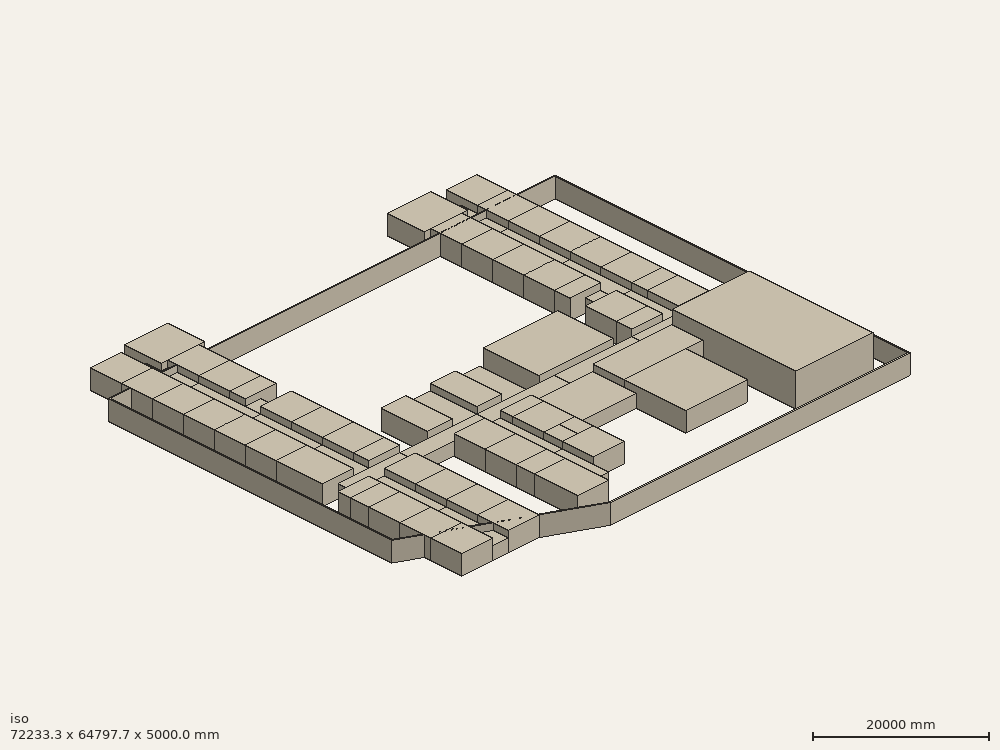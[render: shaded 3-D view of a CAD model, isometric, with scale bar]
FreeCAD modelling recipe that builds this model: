
FCSTD DOCUMENT  (FreeCAD 0.21R33771 (Git))
Label: WFCMaintest
License: All rights reserved
LicenseURL: http://en.wikipedia.org/wiki/All_rights_reserved
objects: Part::Box×79, Part::Compound×20, Sketcher::SketchObject×1, Part::FeaturePython×1
note: 101 computed .brp shape members not serialized (recipe doc carries the construction recipe); baked Part::Feature solids carry a one-line shape summary decoded from their .brp

FEATURE [Part::Box] Box  label="Cube"
  AttacherType = Attacher::AttachEngine3D
  Height = 3000
  Length = 5000
  Width = 5000
FEATURE [Part::Box] Box001  label="Cube001"
  AttacherType = Attacher::AttachEngine3D
  Height = 2000
  Length = 2500
  Placement = pos=(5000,0,0) rot=(0,0,1;0rad)
  Width = 10000
FEATURE [Part::Box] Box002  label="Cube002"
  AttacherType = Attacher::AttachEngine3D
  Height = 3000
  Length = 5000
  Placement = pos=(7500,0,0) rot=(0,0,1;0rad)
  Width = 5000
FEATURE [Part::Box] Box003  label="Cube003"
  AttacherType = Attacher::AttachEngine3D
  Height = 3000
  Length = 5000
  Placement = pos=(0,5000,0) rot=(0,0,1;0rad)
  Width = 5000
FEATURE [Part::Box] Box004  label="Cube004"
  AttacherType = Attacher::AttachEngine3D
  Height = 3000
  Length = 5000
  Placement = pos=(7500,5000,0) rot=(0,0,1;0rad)
  Width = 5000
FEATURE [Part::Compound] Compound  label="4C1"
  Links = -> [Box004,Box,Box001,Box002,Box003]
  Placement = pos=(0,30000,0) rot=(0,0,1;0rad)
FEATURE [Part::Box] Box005  label="Cube005"
  AttacherType = Attacher::AttachEngine3D
  Height = 3000
  Length = 5000
  Width = 5000
FEATURE [Part::Box] Box006  label="Cube006"
  AttacherType = Attacher::AttachEngine3D
  Height = 2000
  Length = 2500
  Placement = pos=(5000,0,0) rot=(0,0,1;0rad)
  Width = 10000
FEATURE [Part::Box] Box007  label="Cube007"
  AttacherType = Attacher::AttachEngine3D
  Height = 3000
  Length = 5000
  Placement = pos=(7500,0,0) rot=(0,0,1;0rad)
  Width = 5000
FEATURE [Part::Box] Box008  label="Cube008"
  AttacherType = Attacher::AttachEngine3D
  Height = 3000
  Length = 5000
  Placement = pos=(7500,5000,0) rot=(0,0,1;0rad)
  Width = 5000
FEATURE [Part::Box] Box009  label="Cube009"
  AttacherType = Attacher::AttachEngine3D
  Height = 3000
  Length = 5000
  Placement = pos=(0,5000,0) rot=(0,0,1;0rad)
  Width = 3000
FEATURE [Part::Box] Box010  label="Cube010"
  AttacherType = Attacher::AttachEngine3D
  Height = 3000
  Length = 5000
  Placement = pos=(0,8000,0) rot=(0,0,1;0rad)
  Width = 2000
FEATURE [Part::Compound] Compound001  label="3C1T1S"
  Links = -> [Box005,Box006,Box007,Box008,Box009,Box010]
  Placement = pos=(0,10000,0) rot=(0,0,1;0rad)
FEATURE [Part::Box] Box011  label="Cube011"
  AttacherType = Attacher::AttachEngine3D
  Height = 2000
  Length = 10000
  Placement = pos=(2500,0,0) rot=(0,0,1;0rad)
  Width = 2500
FEATURE [Part::Box] Box012  label="Cube012"
  AttacherType = Attacher::AttachEngine3D
  Height = 2000
  Length = 2500
  Placement = pos=(5000,2500,0) rot=(0,0,1;0rad)
  Width = 7500
FEATURE [Part::Box] Box013  label="Cube013"
  AttacherType = Attacher::AttachEngine3D
  Height = 3000
  Length = 5000
  Placement = pos=(0,2500,0) rot=(0,0,1;0rad)
  Width = 7500
FEATURE [Part::Box] Box014  label="Cube014"
  AttacherType = Attacher::AttachEngine3D
  Height = 3000
  Length = 5000
  Placement = pos=(7500,5000,0) rot=(0,0,1;0rad)
  Width = 5000
FEATURE [Part::Box] Box015  label="Cube015"
  AttacherType = Attacher::AttachEngine3D
  Height = 3000
  Length = 5000
  Placement = pos=(7500,2500,0) rot=(0,0,1;0rad)
  Width = 2500
FEATURE [Part::Compound] Compound002  label="T"
  Links = -> [Box011,Box012,Box013,Box014,Box015]
  Placement = pos=(0,20000,0) rot=(0,0,1;0rad)
FEATURE [Part::Box] Box016  label="Cube016"
  AttacherType = Attacher::AttachEngine3D
  Height = 2000
  Length = 10000
  Width = 2500
FEATURE [Part::Box] Box017  label="Cube017"
  AttacherType = Attacher::AttachEngine3D
  Height = 2000
  Length = 2500
  Placement = pos=(5000,2500,0) rot=(0,0,1;0rad)
  Width = 7500
FEATURE [Part::Box] Box018  label="Cube018"
  AttacherType = Attacher::AttachEngine3D
  Height = 3000
  Length = 5000
  Placement = pos=(0,5000,0) rot=(0,0,1;0rad)
  Width = 5000
FEATURE [Part::Box] Box019  label="Cube019"
  AttacherType = Attacher::AttachEngine3D
  Height = 3000
  Length = 5000
  Placement = pos=(7500,2500,0) rot=(0,0,1;0rad)
  Width = 5000
FEATURE [Part::Box] Box020  label="Cube020"
  AttacherType = Attacher::AttachEngine3D
  Height = 3000
  Length = 5000
  Placement = pos=(7500,7500,0) rot=(0,0,1;0rad)
  Width = 2500
FEATURE [Part::Box] Box021  label="Cube021"
  AttacherType = Attacher::AttachEngine3D
  Height = 3000
  Length = 5000
  Placement = pos=(0,2500,0) rot=(0,0,1;0rad)
  Width = 2500
FEATURE [Part::Compound] Compound003  label="TF"
  Links = -> [Box016,Box017,Box018,Box019,Box020,Box021]
  Placement = pos=(50000,20000,0) rot=(0,0,1;0rad)
FEATURE [Part::Box] Box022  label="Cube022"
  AttacherType = Attacher::AttachEngine3D
  Height = 3000
  Length = 5000
  Width = 5000
FEATURE [Part::Box] Box023  label="Cube023"
  AttacherType = Attacher::AttachEngine3D
  Height = 2000
  Length = 2500
  Placement = pos=(5000,0,0) rot=(0,0,1;0rad)
  Width = 10000
FEATURE [Part::Box] Box024  label="Cube024"
  AttacherType = Attacher::AttachEngine3D
  Height = 3000
  Length = 5000
  Placement = pos=(7500,2500,0) rot=(0,0,1;0rad)
  Width = 2500
FEATURE [Part::Box] Box025  label="Cube025"
  AttacherType = Attacher::AttachEngine3D
  Height = 3000
  Length = 5000
  Placement = pos=(0,5000,0) rot=(0,0,1;0rad)
  Width = 5000
FEATURE [Part::Box] Box026  label="Cube026"
  AttacherType = Attacher::AttachEngine3D
  Height = 3000
  Length = 5000
  Placement = pos=(7500,5000,0) rot=(0,0,1;0rad)
  Width = 5000
FEATURE [Part::Box] Box027  label="Cube027"
  AttacherType = Attacher::AttachEngine3D
  Height = 2000
  Length = 2500
  Placement = pos=(7500,0,0) rot=(0,0,1;0rad)
  Width = 2500
FEATURE [Part::Compound] Compound004  label="3C1S"
  Links = -> [Box026,Box022,Box023,Box024,Box025,Box027]
  Placement = pos=(0,40000,0) rot=(0,0,1;0rad)
FEATURE [Part::Box] Box028  label="Cube028"
  AttacherType = Attacher::AttachEngine3D
  Height = 3000
  Length = 5000
  Placement = pos=(7500,0,0) rot=(0,0,1;0rad)
  Width = 5000
FEATURE [Part::Box] Box029  label="Cube029"
  AttacherType = Attacher::AttachEngine3D
  Height = 2000
  Length = 2500
  Placement = pos=(5000,0,0) rot=(0,0,1;0rad)
  Width = 10000
FEATURE [Part::Box] Box030  label="Cube030"
  AttacherType = Attacher::AttachEngine3D
  Height = 3000
  Length = 5000
  Placement = pos=(0,2500,0) rot=(0,0,1;0rad)
  Width = 2500
FEATURE [Part::Box] Box031  label="Cube031"
  AttacherType = Attacher::AttachEngine3D
  Height = 3000
  Length = 5000
  Placement = pos=(0,5000,0) rot=(0,0,1;0rad)
  Width = 5000
FEATURE [Part::Box] Box032  label="Cube032"
  AttacherType = Attacher::AttachEngine3D
  Height = 3000
  Length = 5000
  Placement = pos=(7500,5000,0) rot=(0,0,1;0rad)
  Width = 5000
FEATURE [Part::Box] Box033  label="Cube033"
  AttacherType = Attacher::AttachEngine3D
  Height = 2000
  Length = 2500
  Placement = pos=(2500,0,0) rot=(0,0,1;0rad)
  Width = 2500
FEATURE [Part::Compound] Compound005  label="3C1SF"
  Links = -> [Box032,Box028,Box029,Box030,Box031,Box033]
  Placement = pos=(50000,30000,0) rot=(0,0,1;0rad)
FEATURE [Part::Box] Box034  label="Cube034"
  AttacherType = Attacher::AttachEngine3D
  Height = 3000
  Length = 5000
  Width = 5000
FEATURE [Part::Box] Box035  label="Cube035"
  AttacherType = Attacher::AttachEngine3D
  Height = 2000
  Length = 2500
  Placement = pos=(5000,0,0) rot=(0,0,1;0rad)
  Width = 7500
FEATURE [Part::Box] Box036  label="Cube036"
  AttacherType = Attacher::AttachEngine3D
  Height = 3000
  Length = 5000
  Placement = pos=(7500,0,0) rot=(0,0,1;0rad)
  Width = 5000
FEATURE [Part::Box] Box037  label="Cube037"
  AttacherType = Attacher::AttachEngine3D
  Height = 3000
  Length = 5000
  Placement = pos=(0,5000,0) rot=(0,0,1;0rad)
  Width = 5000
FEATURE [Part::Box] Box038  label="Cube038"
  AttacherType = Attacher::AttachEngine3D
  Height = 3000
  Length = 7000
  Placement = pos=(6500,5000,0) rot=(0,0,1;0rad)
  Width = 6000
FEATURE [Part::Compound] Compound006  label="2C1L1A"
  Links = -> [Box038,Box034,Box035,Box036,Box037]
  Placement = pos=(0,50000,0) rot=(0,0,1;0rad)
FEATURE [Part::Box] Box039  label="Cube039"
  AttacherType = Attacher::AttachEngine3D
  Height = 3000
  Length = 5000
  Width = 5000
FEATURE [Part::Box] Box040  label="Cube040"
  AttacherType = Attacher::AttachEngine3D
  Height = 2000
  Length = 2500
  Placement = pos=(5000,0,0) rot=(0,0,1;0rad)
  Width = 7500
FEATURE [Part::Box] Box041  label="Cube041"
  AttacherType = Attacher::AttachEngine3D
  Height = 3000
  Length = 5000
  Placement = pos=(7500,0,0) rot=(0,0,1;0rad)
  Width = 5000
FEATURE [Part::Box] Box042  label="Cube042"
  AttacherType = Attacher::AttachEngine3D
  Height = 3000
  Length = 5000
  Placement = pos=(7500,5000,0) rot=(0,0,1;0rad)
  Width = 5000
FEATURE [Part::Box] Box043  label="Cube043"
  AttacherType = Attacher::AttachEngine3D
  Height = 3000
  Length = 7000
  Placement = pos=(-1000,5000,0) rot=(0,0,1;0rad)
  Width = 6000
FEATURE [Part::Compound] Compound007  label="2C1L1AF"
  Links = -> [Box043,Box039,Box040,Box041,Box042]
  Placement = pos=(50000,50000,0) rot=(0,0,1;0rad)
FEATURE [Part::Box] Box044  label="Cube044"
  AttacherType = Attacher::AttachEngine3D
  Height = 2000
  Length = 12500
  Width = 2500
FEATURE [Part::Box] Box045  label="Cube045"
  AttacherType = Attacher::AttachEngine3D
  Height = 2000
  Length = 4000
  Placement = pos=(8500,2500,0) rot=(0,0,1;0rad)
  Width = 7500
FEATURE [Part::Box] Box046  label="Cube046"
  AttacherType = Attacher::AttachEngine3D
  Height = 3000
  Length = 4000
  Placement = pos=(4500,2500,0) rot=(0,0,1;0rad)
  Width = 7500
FEATURE [Part::Compound] Compound008  label="2L"
  Links = -> [Box044,Box045,Box046]
  Placement = pos=(12500,20000,0) rot=(0,0,1;0rad)
FEATURE [Part::Box] Box047  label="Cube047"
  AttacherType = Attacher::AttachEngine3D
  Height = 2000
  Length = 12500
  Width = 2500
FEATURE [Part::Box] Box048  label="Cube048"
  AttacherType = Attacher::AttachEngine3D
  Height = 2000
  Length = 4000
  Placement = pos=(4000,2500,0) rot=(0,0,1;0rad)
  Width = 7500
FEATURE [Part::Box] Box049  label="Cube049"
  AttacherType = Attacher::AttachEngine3D
  Height = 3000
  Length = 4000
  Placement = pos=(0,2500,0) rot=(0,0,1;0rad)
  Width = 7500
FEATURE [Part::Compound] Compound009  label="2LF"
  Links = -> [Box047,Box048,Box049]
  Placement = pos=(25000,20000,0) rot=(0,0,1;0rad)
FEATURE [Part::Box] Box050  label="Cube050"
  AttacherType = Attacher::AttachEngine3D
  Height = 2000
  Length = 1250
  Placement = pos=(11250,0,0) rot=(0,0,1;0rad)
  Width = 10000
FEATURE [Part::Box] Box051  label="Cube051"
  AttacherType = Attacher::AttachEngine3D
  Height = 3000
  Length = 5000
  Placement = pos=(6275,5000,0) rot=(0,0,1;0rad)
  Width = 5000
FEATURE [Part::Box] Box052  label="Cube052"
  AttacherType = Attacher::AttachEngine3D
  Height = 3000
  Length = 5000
  Placement = pos=(6275,0,0) rot=(0,0,1;0rad)
  Width = 5000
FEATURE [Part::Compound] Compound010  label="2LV"
  Links = -> [Box050,Box051,Box052]
  Placement = pos=(12500,10000,0) rot=(0,0,1;0rad)
FEATURE [Part::Box] Box053  label="Cube053"
  AttacherType = Attacher::AttachEngine3D
  Height = 2000
  Length = 1250
  Placement = pos=(11250,2500,0) rot=(0,0,1;0rad)
  Width = 7500
FEATURE [Part::Box] Box054  label="Cube054"
  AttacherType = Attacher::AttachEngine3D
  Height = 3000
  Length = 5000
  Placement = pos=(6275,7000,0) rot=(0,0,1;0rad)
  Width = 3000
FEATURE [Part::Box] Box055  label="Cube055"
  AttacherType = Attacher::AttachEngine3D
  Height = 3000
  Length = 5000
  Placement = pos=(6275,0,0) rot=(0,0,1;0rad)
  Width = 7000
FEATURE [Part::Compound] Compound011  label="2LVE"
  Links = -> [Box053,Box054,Box055]
  Placement = pos=(12500,0,0) rot=(0,0,1;0rad)
FEATURE [Part::Box] Box056  label="Cube056"
  AttacherType = Attacher::AttachEngine3D
  Height = 2000
  Length = 1250
  Width = 10000
FEATURE [Part::Box] Box057  label="Cube057"
  AttacherType = Attacher::AttachEngine3D
  Height = 3000
  Length = 5000
  Placement = pos=(1250,8000,0) rot=(0,0,1;0rad)
  Width = 2000
FEATURE [Part::Box] Box058  label="Cube058"
  AttacherType = Attacher::AttachEngine3D
  Height = 3000
  Length = 5000
  Placement = pos=(1250,3000,0) rot=(0,0,1;0rad)
  Width = 5000
FEATURE [Part::Box] Box059  label="Cube059"
  AttacherType = Attacher::AttachEngine3D
  Height = 3000
  Length = 2500
  Placement = pos=(1250,0,0) rot=(0,0,1;0rad)
  Width = 3000
FEATURE [Part::Box] Box060  label="Cube060"
  AttacherType = Attacher::AttachEngine3D
  Height = 3000
  Length = 2500
  Placement = pos=(3750,0,0) rot=(0,0,1;0rad)
  Width = 3000
FEATURE [Part::Compound] Compound012  label="2LVF"
  Links = -> [Box056,Box057,Box058,Box059,Box060]
  Placement = pos=(25000,10000,0) rot=(0,0,1;0rad)
FEATURE [Part::Box] Box061  label="Cube061"
  AttacherType = Attacher::AttachEngine3D
  Height = 2000
  Length = 1250
  Placement = pos=(0,2500,0) rot=(0,0,1;0rad)
  Width = 7500
FEATURE [Part::Box] Box062  label="Cube062"
  AttacherType = Attacher::AttachEngine3D
  Height = 3000
  Length = 5000
  Placement = pos=(1250,5000,0) rot=(0,0,1;0rad)
  Width = 5000
FEATURE [Part::Compound] Compound013  label="2LVEF"
  Links = -> [Box061,Box062]
  Placement = pos=(25000,0,0) rot=(0,0,1;0rad)
FEATURE [Part::Box] Box063  label="Cube063"
  AttacherType = Attacher::AttachEngine3D
  Height = 2000
  Length = 12500
  Width = 2500
FEATURE [Part::Box] Box065  label="Cube065"
  AttacherType = Attacher::AttachEngine3D
  Height = 3000
  Length = 12000
  Placement = pos=(-2500,2500,0) rot=(0,0,1;0rad)
  Width = 9000
FEATURE [Part::Compound] Compound014  label="Lib"
  Links = -> [Box063,Box065]
  Placement = pos=(37500,20000,0) rot=(0,0,1;0rad)
FEATURE [Part::Box] Box066  label="Cube066"
  AttacherType = Attacher::AttachEngine3D
  Height = 5000
  Length = 12500
  Placement = pos=(4000,-10000,0) rot=(0,0,1;0rad)
  Width = 20000
FEATURE [Part::Compound] Compound015  label="MPH"
  Links = -> [Box066]
  Placement = pos=(50000,10000,0) rot=(0,0,1;0rad)
FEATURE [Part::Box] Box068  label="Cube068"
  AttacherType = Attacher::AttachEngine3D
  Height = 2000
  Length = 10000
  Placement = pos=(-6250,3000,0) rot=(0,0,1;0rad)
  Width = 7000
FEATURE [Part::Box] Box069  label="Cube069"
  AttacherType = Attacher::AttachEngine3D
  Height = 3000
  Length = 12750
  Placement = pos=(3750,5000,0) rot=(0,0,1;0rad)
  Width = 5000
FEATURE [Part::Box] Box070  label="Cube070"
  AttacherType = Attacher::AttachEngine3D
  Height = 3000
  Length = 10000
  Placement = pos=(3750,-5000,0) rot=(0,0,1;0rad)
  Width = 10000
FEATURE [Part::Compound] Compound016  label="2A"
  Links = -> [Box068,Box069,Box070]
  Placement = pos=(37500,10000,0) rot=(0,0,1;0rad)
FEATURE [Part::Box] Box071  label="Cube071"
  AttacherType = Attacher::AttachEngine3D
  Height = 3000
  Length = 5000
  Width = 5000
FEATURE [Part::Box] Box072  label="Cube072"
  AttacherType = Attacher::AttachEngine3D
  Height = 2000
  Length = 2500
  Placement = pos=(5000,0,0) rot=(0,0,1;0rad)
  Width = 10000
FEATURE [Part::Box] Box073  label="Cube073"
  AttacherType = Attacher::AttachEngine3D
  Height = 3000
  Length = 5000
  Placement = pos=(7500,0,0) rot=(0,0,1;0rad)
  Width = 5000
FEATURE [Part::Box] Box074  label="Cube074"
  AttacherType = Attacher::AttachEngine3D
  Height = 3000
  Length = 5000
  Placement = pos=(0,5000,0) rot=(0,0,1;0rad)
  Width = 5000
FEATURE [Part::Box] Box075  label="Cube075"
  AttacherType = Attacher::AttachEngine3D
  Height = 3000
  Length = 5000
  Placement = pos=(7500,5000,0) rot=(0,0,1;0rad)
  Width = 5000
FEATURE [Part::Compound] Compound017  label="4C2"
  Links = -> [Box075,Box071,Box072,Box073,Box074]
FEATURE [Part::Box] Box076  label="Cube076"
  AttacherType = Attacher::AttachEngine3D
  Height = 3000
  Length = 5000
  Width = 5000
FEATURE [Part::Box] Box077  label="Cube077"
  AttacherType = Attacher::AttachEngine3D
  Height = 2000
  Length = 2500
  Placement = pos=(5000,0,0) rot=(0,0,1;0rad)
  Width = 10000
FEATURE [Part::Box] Box078  label="Cube078"
  AttacherType = Attacher::AttachEngine3D
  Height = 3000
  Length = 5000
  Placement = pos=(7500,0,0) rot=(0,0,1;0rad)
  Width = 5000
FEATURE [Part::Box] Box079  label="Cube079"
  AttacherType = Attacher::AttachEngine3D
  Height = 3000
  Length = 5000
  Placement = pos=(0,5000,0) rot=(0,0,1;0rad)
  Width = 5000
FEATURE [Part::Box] Box080  label="Cube080"
  AttacherType = Attacher::AttachEngine3D
  Height = 3000
  Length = 5000
  Placement = pos=(7500,5000,0) rot=(0,0,1;0rad)
  Width = 5000
FEATURE [Part::Compound] Compound018  label="4CF"
  Links = -> [Box080,Box076,Box077,Box078,Box079]
  Placement = pos=(50000,40000,0) rot=(0,0,1;0rad)
FEATURE [Part::Compound] Compound019
  Links = -> [Compound,Compound001,Compound002,Compound003,Compound004,Compound005,Compound006,Compound007,Compound008,Compound009,Compound010,Compound011,Compound012,Compound013,Compound014,Compound015,Compound016,Compound017,Compound018]
FEATURE [Sketcher::SketchObject] Sketch
  FullyConstrained = false
  sketch-geometry (5):
    g0: LineSegment StartX=68624.6 StartY=-3697.72 StartZ=0 EndX=68624.6 EndY=53528.2 EndZ=0
    g1: LineSegment StartX=-3408.7 StartY=53528.2 StartZ=0 EndX=-3408.7 EndY=7844.49 EndZ=0
    g2: LineSegment StartX=-3408.7 StartY=53528.2 StartZ=0 EndX=68624.6 EndY=53528.2 EndZ=0
    g3: LineSegment StartX=68624.6 StartY=-3697.72 StartZ=0 EndX=20321.4 EndY=-3697.72 EndZ=0
    g4: LineSegment StartX=20321.4 StartY=-3697.72 StartZ=0 EndX=-3408.7 EndY=7844.49 EndZ=0
  constraints (9):
    c: Vertical(g1)
    c: Vertical(g0)
    c: Coincident(g2,g1)
    c: Horizontal(g2)
    c: Coincident(g3,g0)
    c: Horizontal(g3)
    c: Coincident(g4,g3)
    c: Coincident(g4,g1)
    c: Coincident(g2,g0)
FEATURE [Part::FeaturePython] Wall  # Arch/BIM 166 (typed FeaturePython)
  Align = 2
  Area = 7.48903e+08
  Base = -> Sketch
  BlockHeight = 0
  BlockLength = 0
  CountBroken = 0
  CountEntire = 0
  Face = 0
  Height = 3000
  HorizontalArea = 4.99269e+07
  IfcData = attributes={"GlobalId": {"name": "GlobalId", "type": "IfcGloballyUniqueId", "is_enum": false, "enum_values": []}, "Description": {"... (+533 chars omitted),+1 more (map truncated)
  IfcType = 166
  Joint = 0
  Length = 249634
  MakeBlocks = false
  MoveBase = false
  MoveWithHost = false
  Normal = (0,0,0)
  OffsetFirst = 0
  OffsetSecond = 0
  PerimeterLength = 250406
  PredefinedType = 0
  VerticalArea = 1.49781e+09
  Width = 200
